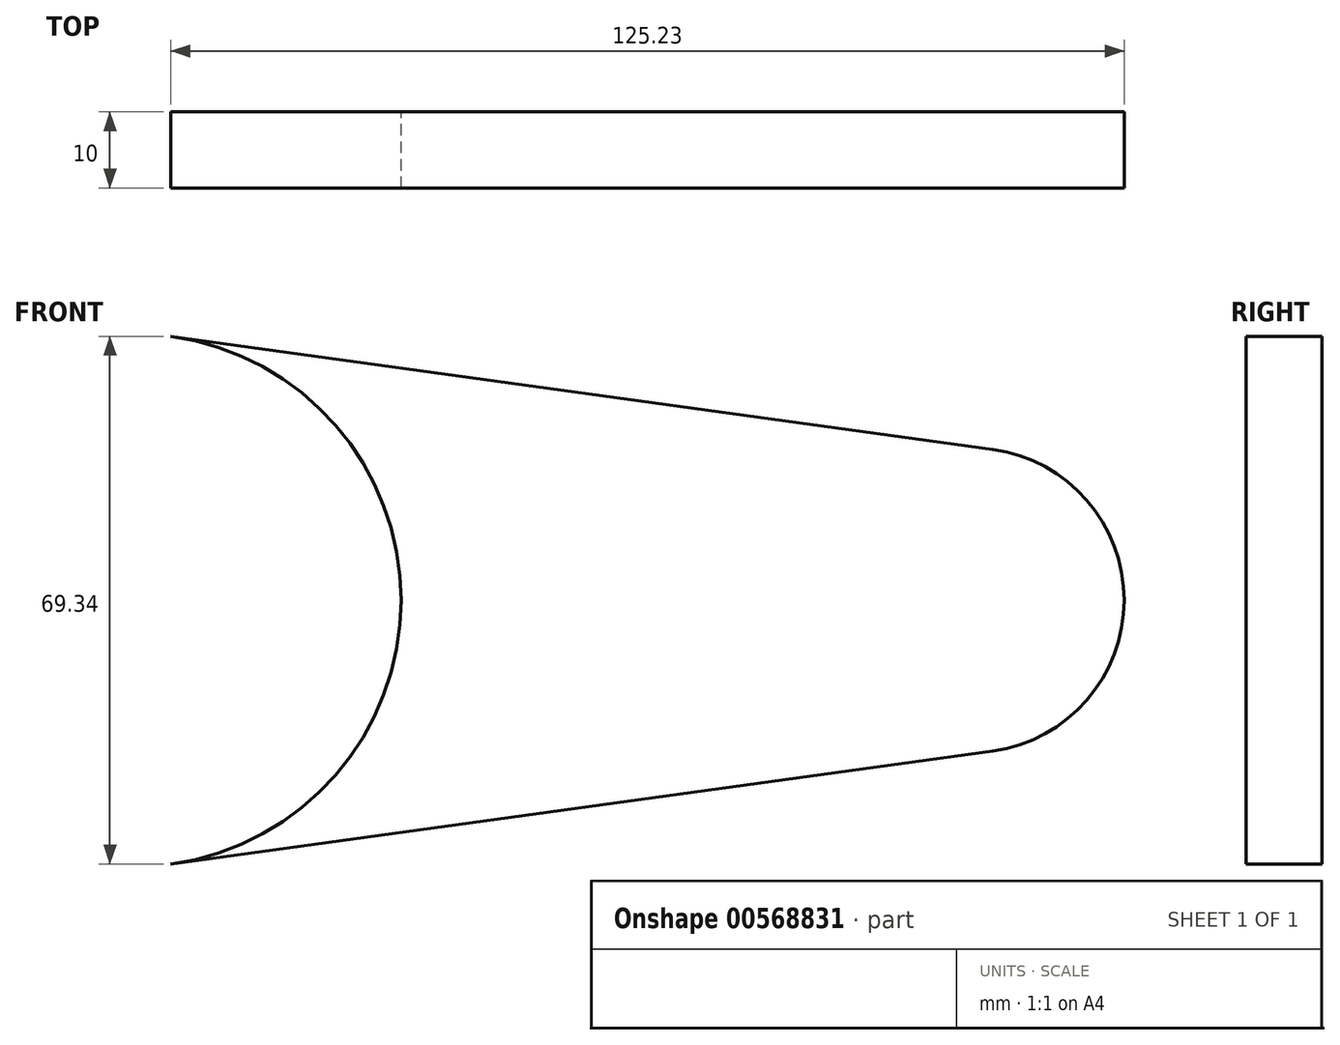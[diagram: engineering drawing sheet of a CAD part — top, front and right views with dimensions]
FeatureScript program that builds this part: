
annotation { "Feature Type Name" : "Feature", "Feature Type Description" : "" }
export const myFeature = defineFeature(function(context is Context, id is Id, definition is map)
    precondition{}
    {
        {
            var Q0;
            Q0=qCreatedBy(makeId("Front.planeOp"),FACE);
            var sketch = newSketch(context, id + "F0", { "sketchPlane" : qUnion([Q0])});
            skCircle(sketch, "E0", {"center": v(0, 0) * mm, "radius": 35 * mm});
            skCircle(sketch, "E1", {"center": v(110, 0) * mm, "radius": 20 * mm});
            skLineSegment(sketch, "E2", {"start": v(4.77, 34.67) * mm, "end": v(112.73, 19.81) * mm});
            skLineSegment(sketch, "E3", {"start": v(4.77, -34.67) * mm, "end": v(112.73, -19.81) * mm});
            skSolve(sketch);
        }
        {
            var Q0;
            {var subQ0=sQuery(id+"F0.wireOp",EDGE,"E2");Q0=makeQuery(id+"F0.imprint","IMPRINT",FACE,{"disambiguationData":[TD([[makeQuery(id+"F0.imprint","IMPRINT",EDGE,{"derivedFrom":subQ0}),-1.0]])]});}
            var Q1;
            {var subQ0=sQuery(id+"F0.wireOp",EDGE,"E1");var subQ1=makeQuery(id+"F0.imprint","INTERSECT",VERTEX,{"derivedFrom":[subQ0,sQuery(id+"F0.wireOp",EDGE,"E2")]});Q1=makeQuery(id+"F0.imprint","IMPRINT",FACE,{"disambiguationData":[TD([[makeQuery(id+"F0.imprint","IMPRINT",EDGE,{"disambiguationData":[TD([[subQ1,-1.0]])],"derivedFrom":subQ0}),1.0]])]});}
            extrude(context, id + "F1", {"entities" : qUnion([Q0, Q1]), "depth" : 10 * mm, "offsetDistance" : 25 * mm});
        }
    });
